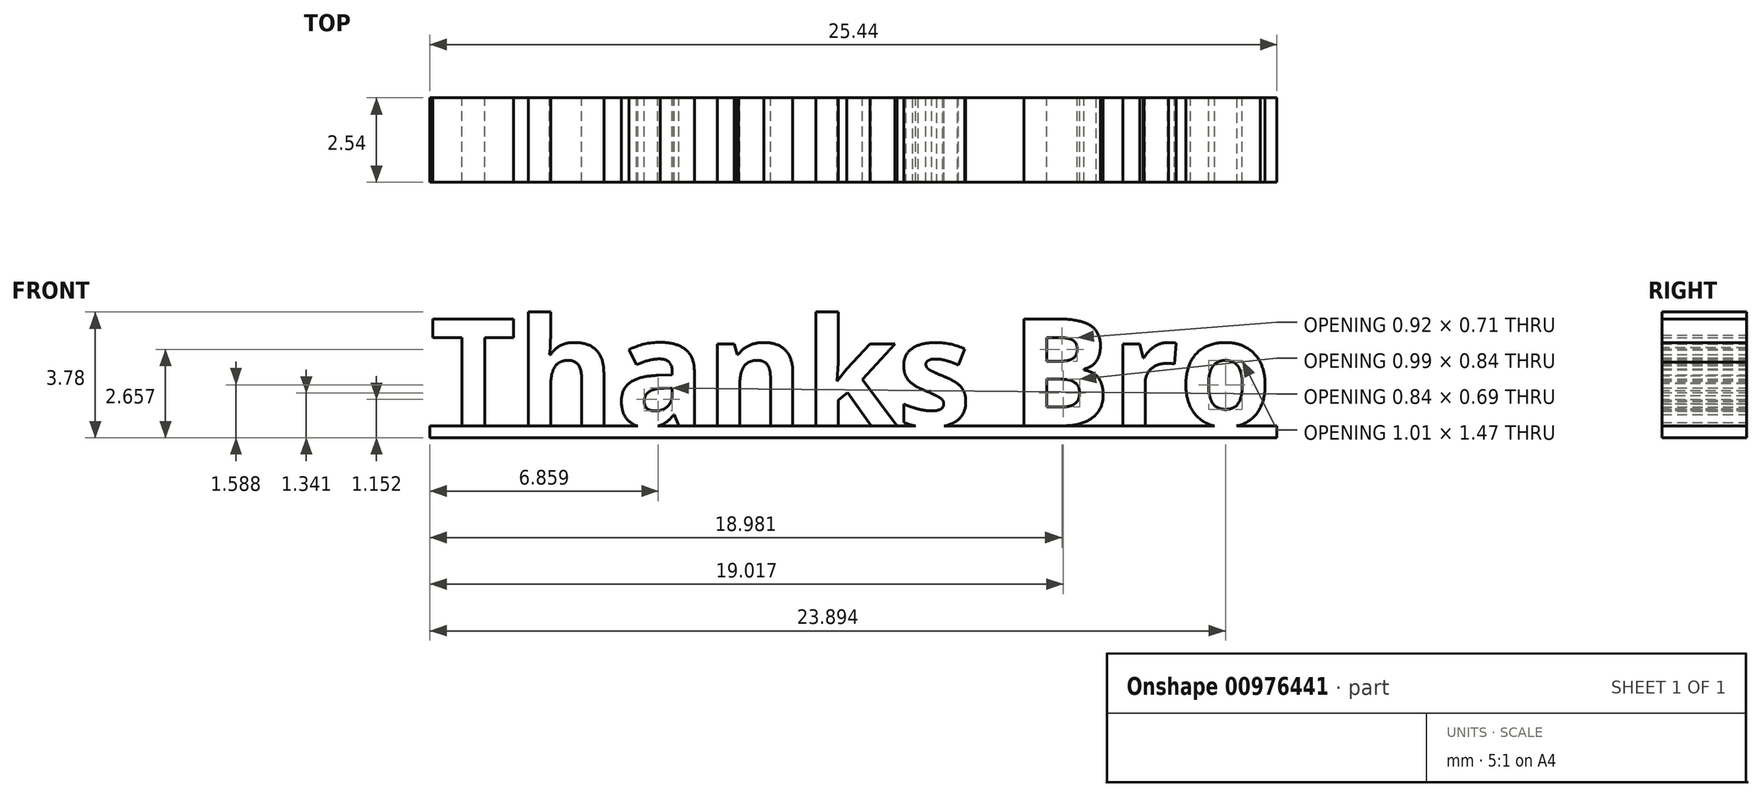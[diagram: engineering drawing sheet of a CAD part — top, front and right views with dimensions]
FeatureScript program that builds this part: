
annotation { "Feature Type Name" : "Feature", "Feature Type Description" : "" }
export const myFeature = defineFeature(function(context is Context, id is Id, definition is map)
    precondition{}
    {
        {
            var Q0;
            Q0=qCreatedBy(makeId("Front.planeOp"),FACE);
            var sketch = newSketch(context, id + "F0", { "sketchPlane" : qUnion([Q0])});
            skText(sketch, "E0", { "text": "Thanks Bro", "fontName": "OpenSans-Bold.ttf"});
            skLineSegment(sketch, "E1.bottom", {"start": v(-21.66, 1.5) * mm, "end": v(3.78, 1.5) * mm});
            skLineSegment(sketch, "E1.top", {"start": v(-21.66, 1.14) * mm, "end": v(3.78, 1.14) * mm});
            skLineSegment(sketch, "E1.left", {"start": v(-21.66, 1.5) * mm, "end": v(-21.66, 1.14) * mm});
            skLineSegment(sketch, "E1.right", {"start": v(3.78, 1.5) * mm, "end": v(3.78, 1.14) * mm});
            const initialGuessF0  = {"E0": [-0.02166, 0.0015, 1, 0, 0.00324]};
            skSetInitialGuess(sketch, initialGuessF0);
            skSolve(sketch);
        }
        {
            var Q0;
            Q0 = qSketchRegion(id + "F0", true);
            extrude(context, id + "F1", {"entities" : qUnion([Q0]), "depth" : 2.54 * mm, "offsetDistance" : 25.4 * mm});
        }
    });
